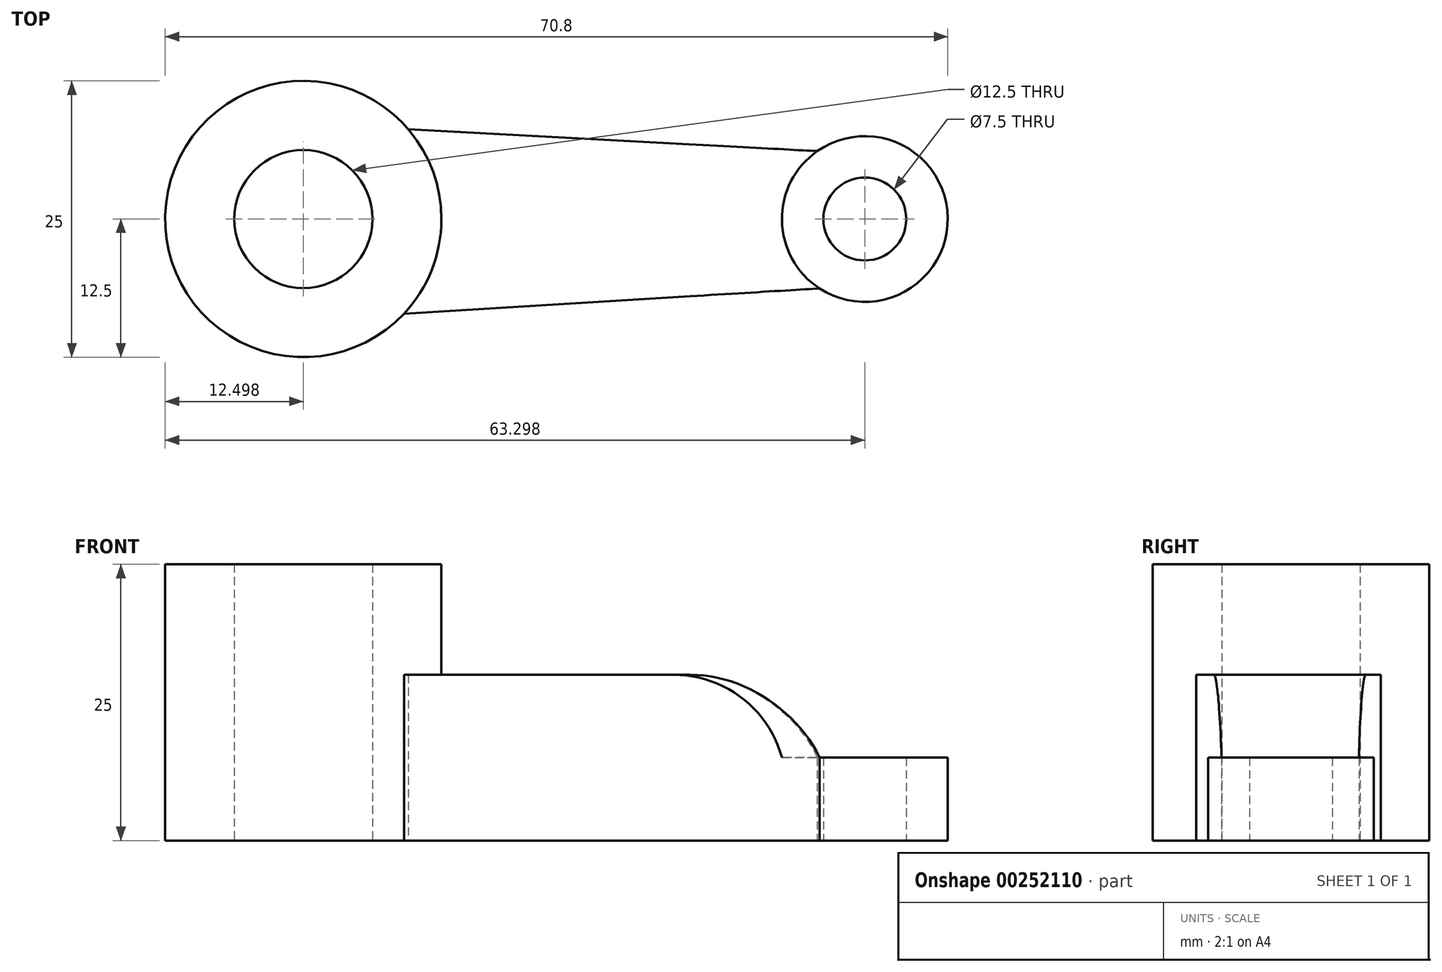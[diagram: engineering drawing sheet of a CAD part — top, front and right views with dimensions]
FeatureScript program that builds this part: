
annotation { "Feature Type Name" : "Feature", "Feature Type Description" : "" }
export const myFeature = defineFeature(function(context is Context, id is Id, definition is map)
    precondition{}
    {
        {
            var Q0;
            Q0=qCreatedBy(makeId("Top.planeOp"),FACE);
            var sketch = newSketch(context, id + "F0", { "sketchPlane" : qUnion([Q0])});
            skCircle(sketch, "E0", {"center": v(-29.92, 0) * mm, "radius": 6.25 * mm});
            skCircle(sketch, "E1", {"center": v(-29.92, 0) * mm, "radius": 12.5 * mm});
            skCircle(sketch, "E2", {"center": v(20.88, 0) * mm, "radius": 3.75 * mm});
            skCircle(sketch, "E3", {"center": v(20.88, 0) * mm, "radius": 7.5 * mm});
            skLineSegment(sketch, "E4", {"start": v(-20.44, 8.14) * mm, "end": v(16.58, 6.15) * mm});
            skLineSegment(sketch, "E5", {"start": v(-20.81, -8.56) * mm, "end": v(16.78, -6.28) * mm});
            skSolve(sketch);
        }
        {
            var Q0;
            Q0=makeQuery(id+"F0.imprint","IMPRINT",FACE,{"disambiguationData":[TD([[makeQuery(id+"F0.imprint","IMPRINT",EDGE,{"derivedFrom":sQuery(id+"F0.wireOp",EDGE,"E0")}),-1.0]])]});
            extrude(context, id + "F1", {"entities" : qUnion([Q0]), "depth" : 25 * mm});
        }
        {
            var Q0;
            {var subQ0=sQuery(id+"F0.wireOp",EDGE,"E4");Q0=makeQuery(id+"F0.imprint","IMPRINT",FACE,{"disambiguationData":[TD([[makeQuery(id+"F0.imprint","IMPRINT",EDGE,{"derivedFrom":subQ0}),-1.0]])]});}
            extrude(context, id + "F2", {"entities" : qUnion([Q0]), "operationType" : NewBodyOperationType.ADD, "depth" : 15 * mm});
        }
        {
            var Q0;
            Q0=makeQuery(id+"F0.imprint","IMPRINT",FACE,{"disambiguationData":[TD([[makeQuery(id+"F0.imprint","IMPRINT",EDGE,{"derivedFrom":sQuery(id+"F0.wireOp",EDGE,"E2")}),-1.0]])]});
            extrude(context, id + "F3", {"entities" : qUnion([Q0]), "operationType" : NewBodyOperationType.ADD, "depth" : 7.5 * mm});
        }
        {
            var Q0;
            Q0=makeQuery(id+"F2.opExtrude","CAP_EDGE",EDGE,{"disambiguationData":[OSD([sQuery(id+"F0.wireOp",EDGE,"E3")])],"isStart":false});
            fillet(context, id + "F4", {"entities" : qUnion([Q0]), "radius" : 10.14 * mm, "tangentPropagation" : true, "allowEdgeOverflow" : false});
        }
    });
